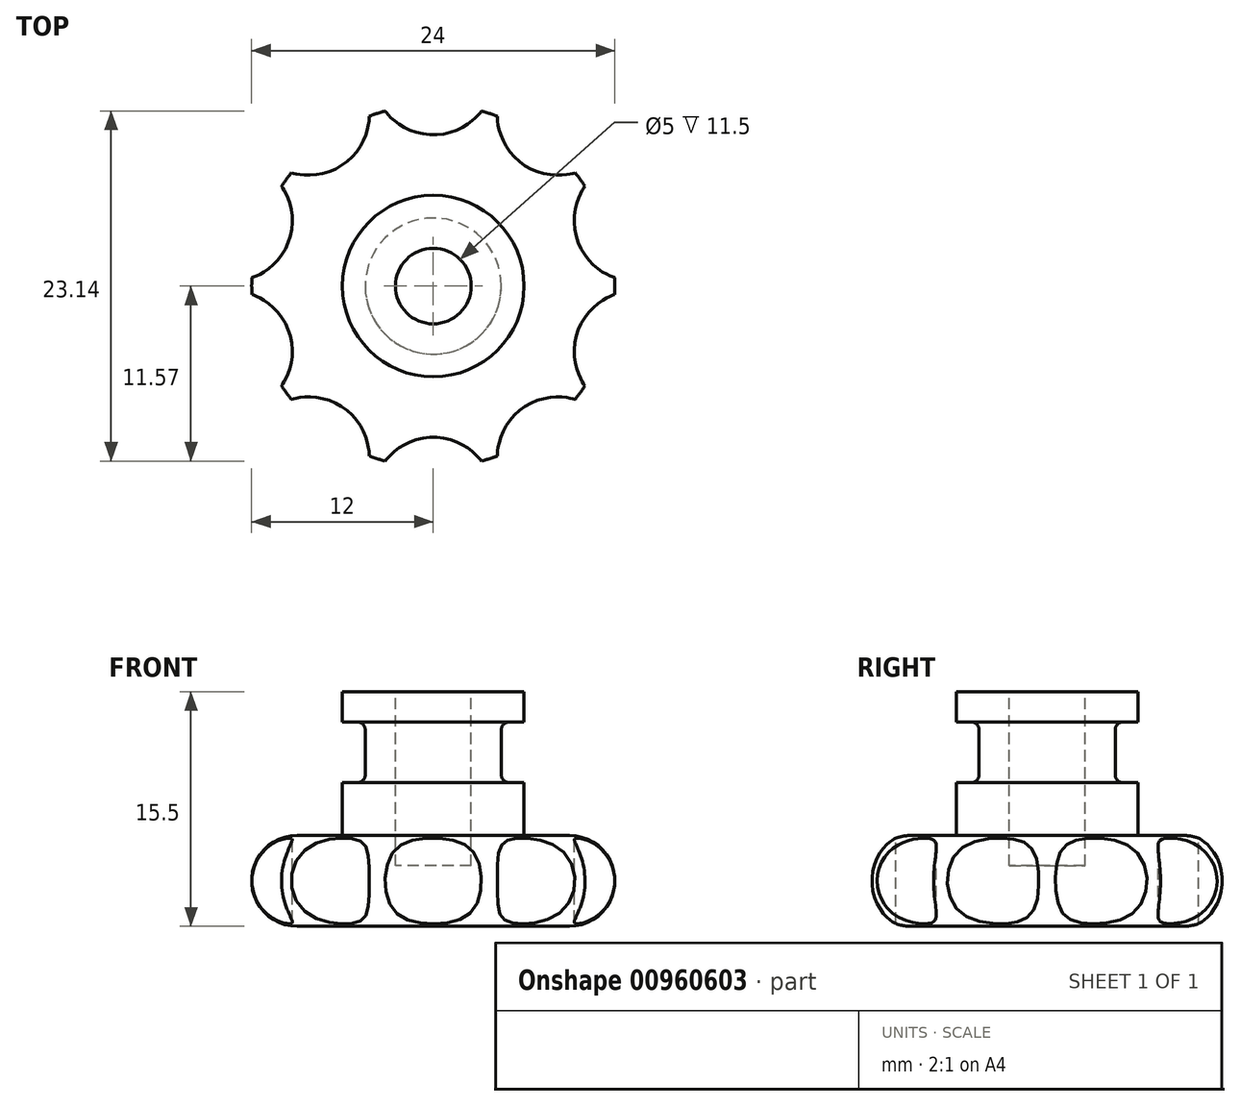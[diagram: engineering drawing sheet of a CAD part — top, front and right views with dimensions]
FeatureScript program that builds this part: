
annotation { "Feature Type Name" : "Feature", "Feature Type Description" : "" }
export const myFeature = defineFeature(function(context is Context, id is Id, definition is map)
    precondition{}
    {
        {
            var Q0;
            Q0=qCreatedBy(makeId("Front.planeOp"),FACE);
            var sketch = newSketch(context, id + "F0", { "sketchPlane" : qUnion([Q0])});
            skLineSegment(sketch, "E0", {"start": v(-2.5, 15.5) * mm, "end": v(-2.5, 4) * mm});
            skLineSegment(sketch, "E1", {"start": v(-2.5, 4) * mm, "end": v(0, 4) * mm});
            skLineSegment(sketch, "E2", {"start": v(0, 4) * mm, "end": v(0, 0) * mm});
            skLineSegment(sketch, "E3", {"start": v(0, 0) * mm, "end": v(-12, 0) * mm});
            skLineSegment(sketch, "E4", {"start": v(-12, 0) * mm, "end": v(-12, 6) * mm});
            skLineSegment(sketch, "E5", {"start": v(-12, 6) * mm, "end": v(-6, 6) * mm});
            skLineSegment(sketch, "E6", {"start": v(-6, 15.5) * mm, "end": v(-2.5, 15.5) * mm});
            skLineSegment(sketch, "E7.bottom", {"start": v(-6, 13.5) * mm, "end": v(-4.5, 13.5) * mm});
            skLineSegment(sketch, "E7.right", {"start": v(-4.5, 13.5) * mm, "end": v(-4.5, 9.5) * mm});
            skLineSegment(sketch, "E8.trimOffspring", {"start": v(-6, 13.5) * mm, "end": v(-6, 15.5) * mm});
            skLineSegment(sketch, "E9", {"start": v(-4.5, 11.5) * mm, "end": v(-6.12, 11.5) * mm, "construction": true});
            skLineSegment(sketch, "E10", {"start": v(-4.5, 9.5) * mm, "end": v(-6, 9.5) * mm});
            skLineSegment(sketch, "E11", {"start": v(-6, 9.5) * mm, "end": v(-6, 6) * mm});
            skSolve(sketch);
        }
        {
            var Q0;
            Q0=makeQuery(id+"F0.imprint","IMPRINT",FACE,{"disambiguationData":[TD([[makeQuery(id+"F0.imprint","IMPRINT",EDGE,{"derivedFrom":sQuery(id+"F0.wireOp",EDGE,"E0")}),-1.0]])]});
            var Q1;
            Q1=sQuery(id+"F0.wireOp",EDGE,"E2");
            revolve(context, id + "F1", {"surfaceOperationType" : NewSurfaceOperationType.NEW, "entities" : qUnion([Q0]), "axis" : qUnion([Q1]), "revolveType" : RevolveType.FULL});
        }
        {
            var Q0;
            Q0=makeQuery(id+"F1.opRevolve","SWEPT_EDGE",EDGE,{"disambiguationData":[OSD([sQuery(id+"F0.wireOp",EDGE,"E4"),sQuery(id+"F0.wireOp",EDGE,"E5")])]});
            var Q1;
            Q1=makeQuery(id+"F1.opRevolve","SWEPT_EDGE",EDGE,{"disambiguationData":[OSD([sQuery(id+"F0.wireOp",EDGE,"E3"),sQuery(id+"F0.wireOp",EDGE,"E4")])]});
            fillet(context, id + "F2", {"entities" : qUnion([Q0, Q1]), "radius" : 3 * mm, "tangentPropagation" : true, "allowEdgeOverflow" : false});
        }
        {
            var Q0;
            Q0=makeQuery(id+"F1.opRevolve","SWEPT_FACE",FACE,{"disambiguationData":[OSD([sQuery(id+"F0.wireOp",EDGE,"E5")])]});
            var sketch = newSketch(context, id + "F3", { "sketchPlane" : qUnion([Q0])});
            skCircle(sketch, "E12", {"center": v(0, 14) * mm, "radius": 4 * mm});
            skCircle(sketch, "E13.1.0", {"center": v(-8.23, 11.33) * mm, "radius": 4 * mm});
            skCircle(sketch, "E13.2.0", {"center": v(-13.31, 4.33) * mm, "radius": 4 * mm});
            skCircle(sketch, "E13.3.0", {"center": v(-13.31, -4.33) * mm, "radius": 4 * mm});
            skCircle(sketch, "E13.4.0", {"center": v(-8.23, -11.33) * mm, "radius": 4 * mm});
            skCircle(sketch, "E13.5.0", {"center": v(0, -14) * mm, "radius": 4 * mm});
            skCircle(sketch, "E13.6.0", {"center": v(8.23, -11.33) * mm, "radius": 4 * mm});
            skCircle(sketch, "E13.7.0", {"center": v(13.31, -4.33) * mm, "radius": 4 * mm});
            skCircle(sketch, "E13.8.0", {"center": v(13.31, 4.33) * mm, "radius": 4 * mm});
            skCircle(sketch, "E13.9.0", {"center": v(8.23, 11.33) * mm, "radius": 4 * mm});
            skPoint(sketch, "E13.center", {"position": v(0, 0) * mm});
            skSolve(sketch);
        }
        {
            var Q0;
            Q0=makeQuery(id+"F3.imprint","IMPRINT",FACE,{"disambiguationData":[TD([[makeQuery(id+"F3.imprint","IMPRINT",EDGE,{"derivedFrom":sQuery(id+"F3.wireOp",EDGE,"E12")}),1.0]])]});
            var Q1;
            Q1=makeQuery(id+"F3.imprint","IMPRINT",FACE,{"disambiguationData":[TD([[makeQuery(id+"F3.imprint","IMPRINT",EDGE,{"derivedFrom":sQuery(id+"F3.wireOp",EDGE,"E13.9.0")}),1.0]])]});
            var Q2;
            Q2=makeQuery(id+"F3.imprint","IMPRINT",FACE,{"disambiguationData":[TD([[makeQuery(id+"F3.imprint","IMPRINT",EDGE,{"derivedFrom":sQuery(id+"F3.wireOp",EDGE,"E13.8.0")}),1.0]])]});
            var Q3;
            Q3=makeQuery(id+"F3.imprint","IMPRINT",FACE,{"disambiguationData":[TD([[makeQuery(id+"F3.imprint","IMPRINT",EDGE,{"derivedFrom":sQuery(id+"F3.wireOp",EDGE,"E13.7.0")}),1.0]])]});
            var Q4;
            Q4=makeQuery(id+"F3.imprint","IMPRINT",FACE,{"disambiguationData":[TD([[makeQuery(id+"F3.imprint","IMPRINT",EDGE,{"derivedFrom":sQuery(id+"F3.wireOp",EDGE,"E13.6.0")}),1.0]])]});
            var Q5;
            Q5=makeQuery(id+"F3.imprint","IMPRINT",FACE,{"disambiguationData":[TD([[makeQuery(id+"F3.imprint","IMPRINT",EDGE,{"derivedFrom":sQuery(id+"F3.wireOp",EDGE,"E13.5.0")}),1.0]])]});
            var Q6;
            Q6=makeQuery(id+"F3.imprint","IMPRINT",FACE,{"disambiguationData":[TD([[makeQuery(id+"F3.imprint","IMPRINT",EDGE,{"derivedFrom":sQuery(id+"F3.wireOp",EDGE,"E13.4.0")}),1.0]])]});
            var Q7;
            Q7=makeQuery(id+"F3.imprint","IMPRINT",FACE,{"disambiguationData":[TD([[makeQuery(id+"F3.imprint","IMPRINT",EDGE,{"derivedFrom":sQuery(id+"F3.wireOp",EDGE,"E13.3.0")}),1.0]])]});
            var Q8;
            Q8=makeQuery(id+"F3.imprint","IMPRINT",FACE,{"disambiguationData":[TD([[makeQuery(id+"F3.imprint","IMPRINT",EDGE,{"derivedFrom":sQuery(id+"F3.wireOp",EDGE,"E13.2.0")}),1.0]])]});
            var Q9;
            Q9=makeQuery(id+"F3.imprint","IMPRINT",FACE,{"disambiguationData":[TD([[makeQuery(id+"F3.imprint","IMPRINT",EDGE,{"derivedFrom":sQuery(id+"F3.wireOp",EDGE,"E13.1.0")}),1.0]])]});
            extrude(context, id + "F4", {"entities" : qUnion([Q0, Q1, Q2, Q3, Q4, Q5, Q6, Q7, Q8, Q9]), "operationType" : NewBodyOperationType.REMOVE, "oppositeDirection" : true, "depth" : 25 * mm, "offsetDistance" : 25 * mm});
        }
        {
            var Q0;
            Q0=makeQuery(id+"F1.opRevolve","SWEPT_EDGE",EDGE,{"disambiguationData":[OSD([sQuery(id+"F0.wireOp",EDGE,"E7.bottom"),sQuery(id+"F0.wireOp",EDGE,"E7.right")])]});
            var Q1;
            Q1=makeQuery(id+"F1.opRevolve","SWEPT_EDGE",EDGE,{"disambiguationData":[OSD([sQuery(id+"F0.wireOp",EDGE,"E7.right"),sQuery(id+"F0.wireOp",EDGE,"E10")])]});
            fillet(context, id + "F5", {"entities" : qUnion([Q0, Q1]), "radius" : .5 * mm, "tangentPropagation" : true, "allowEdgeOverflow" : false});
        }
    });
